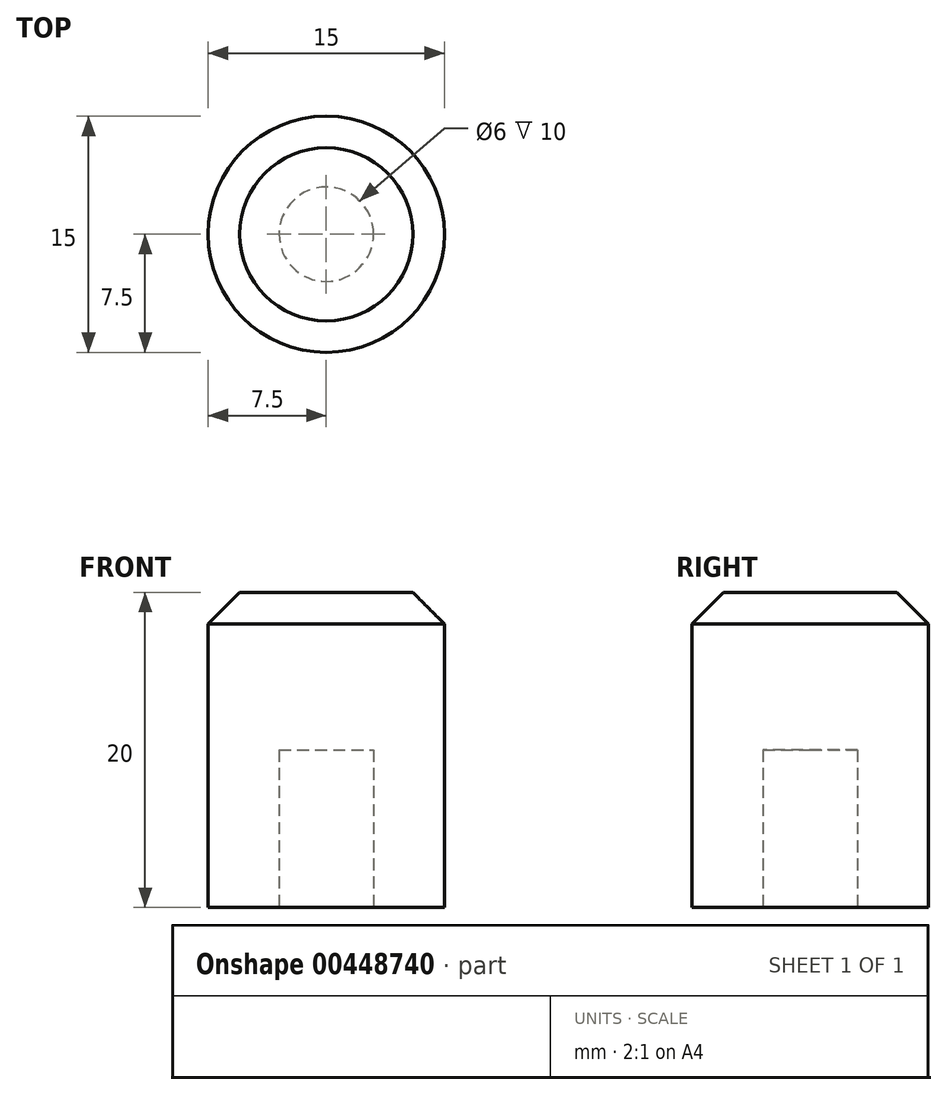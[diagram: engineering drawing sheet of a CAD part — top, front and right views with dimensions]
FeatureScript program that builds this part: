
annotation { "Feature Type Name" : "Feature", "Feature Type Description" : "" }
export const myFeature = defineFeature(function(context is Context, id is Id, definition is map)
    precondition{}
    {
        {
            var Q0;
            Q0=qCreatedBy(makeId("Top.planeOp"),FACE);
            var sketch = newSketch(context, id + "F0", { "sketchPlane" : qUnion([Q0])});
            skCircle(sketch, "E0", {"center": v(0, 0) * mm, "radius": 7.5 * mm});
            skSolve(sketch);
        }
        {
            var Q0;
            Q0 = qSketchRegion(id + "F0", true);
            extrude(context, id + "F1", {"entities" : qUnion([Q0]), "depth" : 20 * mm});
        }
        {
            var Q0;
            Q0=makeQuery(id+"F1.opExtrude","CAP_EDGE",EDGE,{"disambiguationData":[OSD([sQuery(id+"F0.wireOp",EDGE,"E0")])],"isStart":false});
            chamfer(context, id + "F2", {"entities" : qUnion([Q0]), "width" : 2 * mm, "tangentPropagation" : true});
        }
        {
            var Q0;
            Q0=makeQuery(id+"F1.opExtrude","CAP_FACE",FACE,{"disambiguationData":[OSD([sQuery(id+"F0.wireOp",EDGE,"E0")])],"isStart":true});
            var sketch = newSketch(context, id + "F3", { "sketchPlane" : qUnion([Q0])});
            skCircle(sketch, "E1", {"center": v(0, 0) * mm, "radius": 3 * mm});
            skSolve(sketch);
        }
        {
            var Q0;
            Q0 = qSketchRegion(id + "F3", true);
            extrude(context, id + "F4", {"entities" : qUnion([Q0]), "operationType" : NewBodyOperationType.REMOVE, "oppositeDirection" : true, "depth" : 10 * mm});
        }
    });
